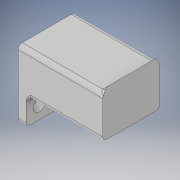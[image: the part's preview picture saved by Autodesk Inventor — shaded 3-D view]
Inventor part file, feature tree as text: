
AUTODESK INVENTOR PART (.ipt)
format: ipt  version: 2018 (Build 220112000, 112)  size: 413,184 bytes
history: native  units: in
note: dims shown in document units (in); Inventor stores cm internally (conversion verified against a paired STEP export)
features: reference x18, extrude x11, sketch x11, fillet x8, other x7, projected_geometry x4, plane x3
ambient origin geometry x8: Origin, YZ Plane, XZ Plane, XY Plane, X Axis, Y Axis, Z Axis, Center Point
bodies: Solid1 (feature_tree)
feature tree (62):
  extrude  "Extrusion1"  Depth=0.125in
  extrude  "Extrusion2"  Depth=0.4724in TaperAngle=0.0deg
  extrude  "Extrusion3"  Depth=0.2in TaperAngle=0.0deg
  extrude  "Extrusion4"  Depth=0.4in
  extrude  "Extrusion5"  Depth=0.25in
  extrude  "Extrusion6"  Depth=0.0787in TaperAngle=0.0deg
  fillet  "Fillet1"  Radius=0.125in
  fillet  "Fillet4"  Radius=0.1181in
  sketch  "Sketch8"  dims[d19=0.125in d20=0.1181in]
  plane  "Work Plane1"
  extrude  "Extrusion7"  Depth=0.1181in
  sketch  "Sketch9"  dims[d21=1.15in d22=0.0787in d23=0.0in d24=0.0394in d27=0.0394in d28=0.0197in d29=0.0197in]
  plane  "Work Plane2"
  extrude  "Extrusion8"  Depth=0.0394in TaperAngle=0.0deg
  fillet  "Fillet5"  Radius=0.0394in
  fillet  "Fillet6"  Radius=0.0394in
  fillet  "Fillet7"  Radius=0.0197in
  fillet  "Fillet9"  Radius=0.0197in
  sketch  "Sketch10"  dims[d30=1.0in d31=0.0in d32=0.0394in d33=0.0394in d34=1.0in d35=0.0in]
  plane  "Work Plane3"
  extrude  "Extrusion9"  Depth=0.0394in
  fillet  "Fillet10"  Radius=0.0394in
  fillet  "Fillet11"  Radius=1.0in
  extrude  "Extrusion10"  Depth=0.0394in
  extrude  "Extrusion11"  Depth=0.0394in
  sketch  "Sketch1"  dims[d0=0.5in d1=0.125in]
  reference  "Reference1"
  reference  "Reference2"
  reference  "Reference3"
  reference  "Reference4"
  reference  "Reference5"
  reference  "Reference6"
  reference  "Reference7"
  reference  "Reference8"
  reference  "Reference9"
  reference  "Reference10"
  reference  "Reference11"
  reference  "Reference12"
  reference  "Reference13"
  reference  "Reference14"
  reference  "Reference15"
  reference  "Reference16"
  reference  "Reference17"
  sketch  "Sketch2"  dims[d2=0.7in d3=0.4724in d4=0.0in]
  projected_geometry  "Projected Loop1"
  projected_geometry  "Projected Loop2"
  sketch  "Sketch4"  dims[d5=0.0787in d6=0.0in d7=0.2in d8=0.0in]
  projected_geometry  "Projected Loop3"
  sketch  "Sketch5"  dims[d9=0.4in d10=0.4in]
  reference  "Reference20"
  sketch  "Sketch6"  dims[d11=0.5512in d12=0.0in d13=0.25in]
  sketch  "Sketch7"  dims[d14=0.25in d15=0.0787in d16=0.0in d17=0.125in d18=0.1181in]
  projected_geometry  "Projected Loop4"
  sketch  "Sketch11"  dims[d36=0.0394in d37=0.0394in]
  sketch  "Sketch12"  dims[d38=0.0394in d40=0.0394in d41=0.0098in d42=1.0in d43=0.0in d44=0.0394in d45=0.0394in d46=12.0in d47=0.0in d48=12.0in d49=0.0in]
  other  "<userpath>\OneDrive\Documents\Inventor\TSA\2018\Animatronics\Tortoise\TurtleAssembly.iam"
  other  "TurtleAssembly.iam"
  other  "servo (2):1"
  other  "smallergear:4"
  other  "<userpath>\OneDrive\Documents\Inventor\TSA\2018\Animatronics\Tortoise\AssemblyTURTLE.iam"
  other  "AssemblyTURTLE.iam"
  other  "Frame:1"
